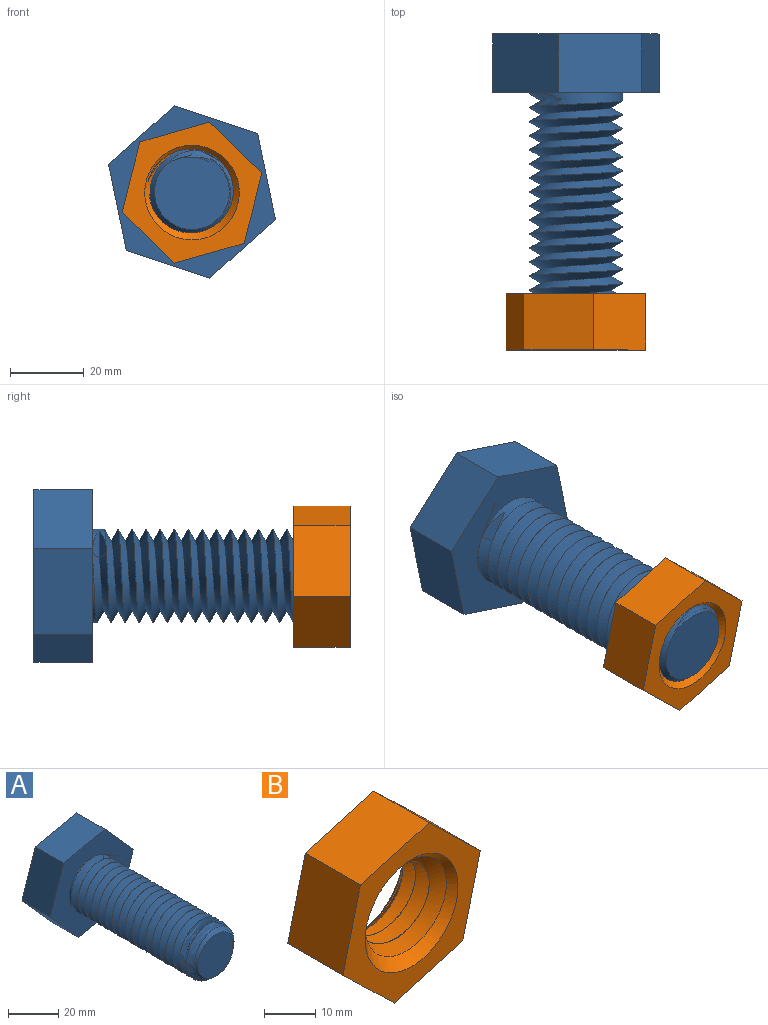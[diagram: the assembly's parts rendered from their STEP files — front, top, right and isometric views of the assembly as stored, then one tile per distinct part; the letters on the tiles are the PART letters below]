
ASSEMBLY  parts=2 mates=1
PART A: 19 faces, bbox 46.9x88.5x45.5 mm
  f0: cylinder r=12.69mm len=63.53mm, axis (0,1,0), area -10.7mm2, adj f3,f12,f14,f16
  f1: cylinder r=12.69mm len=25.38mm, axis (0,1,0), area 126.9mm2, adj f2,f3,f15,f16
  f2: plane 46.67x45.25mm, normal (0,-1,0), area 969.3mm2, adj f1,f4,f5,f6,f7,f8,f9,f13
  f3: bspline ~70.3x25.37mm, area 4707.4mm2, adj f0,f1,f11,f12,f13,f14,f15,f16
  f4: plane 23.34x15.88mm, normal (0.2,0,-0.98), area 378.3mm2, adj f2,f5,f9,f10
  f5: plane 22.62x15.88mm, normal (0.95,0,-0.31), area 378.3mm2, adj f2,f4,f6,f10
  f6: plane 17.79x15.88mm, normal (0.75,0,0.67), area 378.3mm2, adj f2,f5,f7,f10
  f7: plane 23.34x15.88mm, normal (-0.2,0,0.98), area 378.3mm2, adj f2,f6,f8,f10
  f8: plane 22.62x15.88mm, normal (-0.95,0,0.31), area 378.3mm2, adj f2,f7,f9,f10
  f9: plane 17.79x15.88mm, normal (-0.75,0,-0.67), area 378.3mm2, adj f2,f4,f8,f10
  f10: plane 46.67x45.25mm, normal (0,1,0), area 1475.4mm2, adj f4,f5,f6,f7,f8,f9
  f11: plane 20.56x19.91mm, normal (0,-1,0), area 318.1mm2, adj f3,f12,f14
  f12: cone r=10.15mm half-angle=45deg, axis (0,1,0), area 96.1mm2, adj f0,f3,f11,f14
  f13: cylinder r=12.69mm len=0.42mm, axis (0,1,0), area 0mm2, adj f2,f3,f17
  f14: bspline ~71.12x29.3mm, area 4579.5mm2, adj f0,f3,f11,f12,f16
  f15: plane 10.44x7.11mm, normal (0.25,-0.87,0.43), area 22.6mm2, adj f1,f2,f3,f16,f17,f18
  f16: plane 7.41x7.14mm, normal (0.25,0.87,0.43), area 22.2mm2, adj f0,f1,f3,f14,f15
  f17: plane 8.8x5.08mm, normal (-0.5,0,-0.87), area 0.2mm2, adj f2,f13,f15,f18
  f18: plane 0.03x0.02mm, normal (-0.87,0,0.5), area 0mm2, adj f2,f15,f17
PART B: 13 faces, bbox 38x18.4x38.2 mm
  f0: plane 15.24x14.14mm, normal (-0.7,0,-0.72), area 300.5mm2, adj f1,f6,f7,f8
  f1: plane 18.98x15.24mm, normal (0.27,0,-0.96), area 300.5mm2, adj f0,f2,f7,f8
  f2: plane 19.12x15.24mm, normal (0.97,0,-0.25), area 300.5mm2, adj f1,f3,f7,f8
  f3: plane 15.24x14.14mm, normal (0.7,0,0.72), area 300.5mm2, adj f2,f4,f7,f8
  f4: plane 18.98x15.24mm, normal (-0.27,0,0.96), area 300.5mm2, adj f3,f6,f7,f8
  f5: cylinder r=9.01mm len=18.03mm, axis (0,1,0), area 0.4mm2, adj f9,f10,f11,f12
  f6: plane 19.12x15.24mm, normal (-0.97,0,0.25), area 300.5mm2, adj f0,f4,f7,f8
  f7: plane 38.24x37.95mm, normal (0,-1,0), area 493.8mm2, adj f0,f1,f2,f3,f4,f6,f10
  f8: plane 38.24x37.95mm, normal (0,1,0), area 493.8mm2, adj f0,f1,f2,f3,f4,f6,f9
  f9: cone r=12.82mm half-angle=45deg, axis (0,1,0), area 221.7mm2, adj f5,f8,f11,f12
  f10: cone r=9.01mm half-angle=45deg, axis (0,-1,0), area 221.7mm2, adj f5,f7,f11,f12
  f11: bspline ~28.43x24.62mm, area 742.9mm2, adj f5,f9,f10,f12
  f12: bspline ~28.43x24.62mm, area 743.2mm2, adj f5,f9,f10,f11
PLACE A rot(axis=(0,-1,0),90deg) t=(-0.01,0,0.16)mm
PLACE B t=(0,-70.48,-66.25)mm
MATE cylindrical A.f11 <-> B.f5  axis (0,-1,0) through (0,-85.72,0)mm
